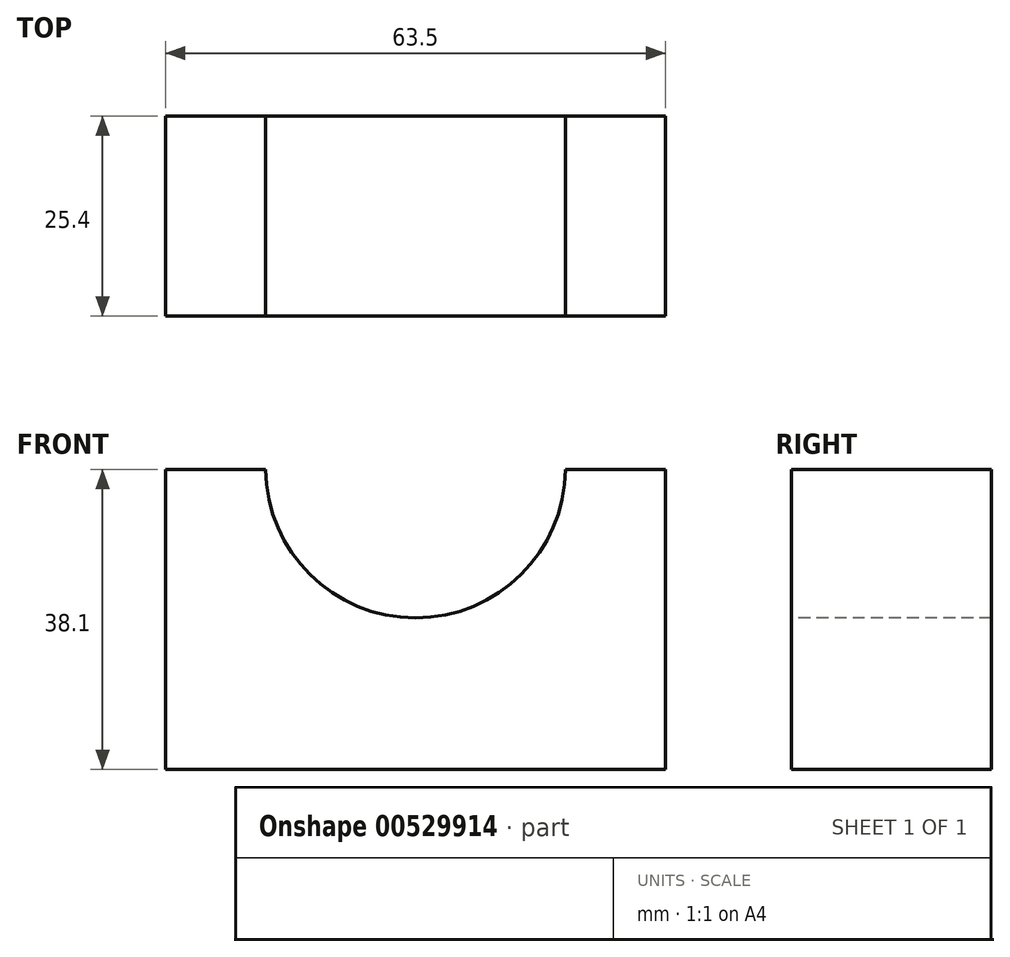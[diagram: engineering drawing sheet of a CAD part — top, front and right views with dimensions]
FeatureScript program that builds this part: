
annotation { "Feature Type Name" : "Feature", "Feature Type Description" : "" }
export const myFeature = defineFeature(function(context is Context, id is Id, definition is map)
    precondition{}
    {
        {
            var Q0;
            Q0=qCreatedBy(makeId("Front.planeOp"),FACE);
            var sketch = newSketch(context, id + "F0", { "sketchPlane" : qUnion([Q0])});
            skLineSegment(sketch, "E0", {"start": v(-65.52, 44.26) * mm, "end": v(-65.52, 6.16) * mm});
            skLineSegment(sketch, "E1", {"start": v(-65.52, 6.16) * mm, "end": v(-2.02, 6.16) * mm});
            skLineSegment(sketch, "E2", {"start": v(-2.02, 6.16) * mm, "end": v(-2.02, 44.26) * mm});
            skLineSegment(sketch, "E3", {"start": v(-2.02, 44.26) * mm, "end": v(-65.52, 44.26) * mm});
            skSolve(sketch);
        }
        {
            var Q0;
            Q0=makeQuery(id+"F0.imprint","IMPRINT",FACE,{"disambiguationData":[TD([[makeQuery(id+"F0.imprint","IMPRINT",EDGE,{"derivedFrom":sQuery(id+"F0.wireOp",EDGE,"E0")}),1.0]])]});
            extrude(context, id + "F1", {"entities" : qUnion([Q0]), "depth" : 25.4 * mm, "offsetDistance" : 25.4 * mm});
        }
        {
            var Q0;
            Q0=makeQuery(id+"F1.opExtrude","CAP_FACE",FACE,{"disambiguationData":[OSD([sQuery(id+"F0.wireOp",EDGE,"E0"),sQuery(id+"F0.wireOp",EDGE,"E1"),sQuery(id+"F0.wireOp",EDGE,"E2"),sQuery(id+"F0.wireOp",EDGE,"E3")])],"isStart":false});
            var sketch = newSketch(context, id + "F2", { "sketchPlane" : qUnion([Q0])});
            skLineSegment(sketch, "E4", {"start": v(-65.52, 44.26) * mm, "end": v(-52.82, 44.26) * mm});
            skLineSegment(sketch, "E5", {"start": v(-2.02, 44.26) * mm, "end": v(-14.72, 44.26) * mm});
            skPoint(sketch, "E6.endSnap0", {"position": v(-33.77, 16.73) * mm});
            skArc(sketch, "E7", {"start": v(-52.82, 44.26) * mm, "mid": v(-33.77, 25.41) * mm, "end": v(-14.72, 44.26) * mm});
            skSolve(sketch);
        }
        {
            var Q0;
            {var subQ0=sQuery(id+"F2.wireOp",EDGE,"E7");Q0=makeQuery(id+"F2.imprint","IMPRINT",FACE,{"disambiguationData":[TD([[makeQuery(id+"F2.imprint","IMPRINT",EDGE,{"derivedFrom":subQ0}),1.0]])]});}
            extrude(context, id + "F3", {"entities" : qUnion([Q0]), "operationType" : NewBodyOperationType.REMOVE, "oppositeDirection" : true, "depth" : 25.4 * mm, "offsetDistance" : 25.4 * mm});
        }
    });
